# Revit family: Storage-Teknion-CESRUS_Recycling_Disposal_Unit_Standard_Bins-R2023
name_source: partatom
category: Furniture
units: mm (PartAtom-declared; Revit-internal decimal feet)

## family parameters
Always vertical = Yes
Cut with Voids When Loaded = No
Enable Cutting in Views = No
OmniClass Number = 23.40.20.00
OmniClass Title = General Furniture and Specialties
Render Appearance Source = Family Geometry
Room Calculation Point = No
Shared = Yes
Work Plane-Based = No

## types (3) — shared parameters
Assembly Code = E2020200
Manufacturer = Teknion
Manufacturer Fax = 416.661.4586
Part Number = CESRUS
Product Documentation Link = https://www.teknion.com
Product Line = Storage Cabinets
Product Page URL = https://www.teknion.com
Series = Expansion Casework+
Sustainability Data = https://www.teknion.com
URL = www.teknion.com
Unit Weight URL = http://www.teknion.com
Warranty = http://www.teknion.com
zero-valued in all types: Default Elevation

## per-type parameters (varying)
- Dual Configuration: 2D - 2 & 4 Bins=Yes; 2D - 3 Bins=No; 2D - 4 Bins=No; Cut - 2 & 4 Doors=2.5 "; Cut - 3 & 4 Doors=0.3 "; Cut - Divider - 1=0.3 "; Cut - Divider - 2=3 "; Cut - Divider - 3=0.3 "; Cut-Out - 2 Bins=1 "; Cut-Out - 3 Bins=0.2 "; Cut-Out - 4 Bins=0.2 "; D - Dual=Yes; Description=Recycling/Disposal Unit - Standard Bins, Dual Configuration, 12" Door Width; Dim 1=8 "; Dim 2=5.75 "; Dim 3=5.085 "; Divider 1=No; Divider 2=Yes; Divider 3=No; Hidden - Divider 1=Yes; Hidden - Divider 2=No; Hidden - Divider 3=Yes; MR - 3 Doors=No; MR - 4 Doors=No; Model=CESRUSD__12____; Q - Quad=No; T - Triple=No; Width=24 "
- Triple Configuration: 2D - 2 & 4 Bins=No; 2D - 3 Bins=Yes; 2D - 4 Bins=No; Cut - 2 & 4 Doors=0.3 "; Cut - 3 & 4 Doors=2.5 "; Cut - Divider - 1=3 "; Cut - Divider - 2=0.3 "; Cut - Divider - 3=3 "; Cut-Out - 2 Bins=0.2 "; Cut-Out - 3 Bins=1.5 "; Cut-Out - 4 Bins=0.2 "; D - Dual=No; Description=Recycling/Disposal Unit - Standard Bins, Triple Configuration, 12" Door Width; Dim 1=6 "; Dim 2=11.667 "; Dim 3=11.085 "; Divider 1=Yes; Divider 2=No; Divider 3=Yes; Hidden - Divider 1=No; Hidden - Divider 2=Yes; Hidden - Divider 3=No; MR - 3 Doors=Yes; MR - 4 Doors=No; Model=CESRUST__12____; Q - Quad=No; T - Triple=Yes; Width=36 "
- Quad Configuration: 2D - 2 & 4 Bins=Yes; 2D - 3 Bins=No; 2D - 4 Bins=Yes; Cut - 2 & 4 Doors=2.5 "; Cut - 3 & 4 Doors=2.5 "; Cut - Divider - 1=3 "; Cut - Divider - 2=3 "; Cut - Divider - 3=3 "; Cut-Out - 2 Bins=1 "; Cut-Out - 3 Bins=0.2 "; Cut-Out - 4 Bins=1 "; D - Dual=No; Description=Recycling/Disposal Unit - Standard Bins, Quad Configuration, 12" Door Width; Dim 1=12 "; Dim 2=5.75 "; Dim 3=5.085 "; Divider 1=Yes; Divider 2=Yes; Divider 3=Yes; Hidden - Divider 1=No; Hidden - Divider 2=No; Hidden - Divider 3=No; MR - 3 Doors=No; MR - 4 Doors=Yes; Model=CESRUSQ__12____; Q - Quad=Yes; T - Triple=No; Width=48 "

## geometry (parser evidence)
native form markers: Sweep x6
no freeform markers — native parametric forms only
